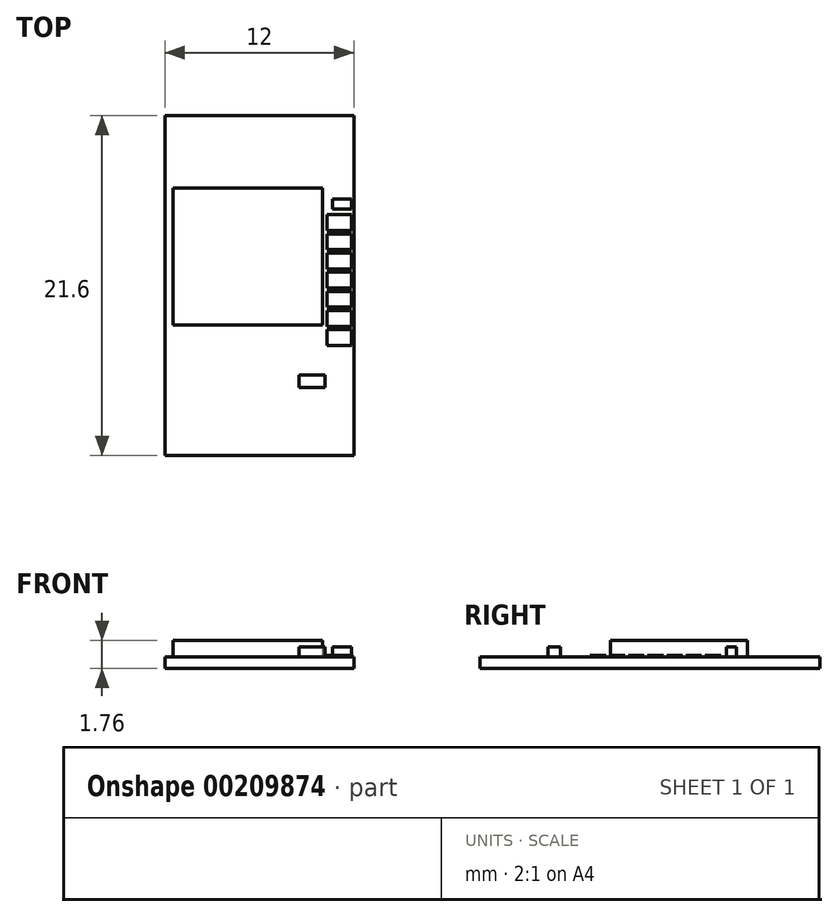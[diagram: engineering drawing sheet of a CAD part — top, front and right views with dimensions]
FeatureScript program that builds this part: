
annotation { "Feature Type Name" : "Feature", "Feature Type Description" : "" }
export const myFeature = defineFeature(function(context is Context, id is Id, definition is map)
    precondition{}
    {
        {
            var Q0;
            Q0=qCreatedBy(makeId("Top.planeOp"),FACE);
            var sketch = newSketch(context, id + "F0", { "sketchPlane" : qUnion([Q0])});
            skLineSegment(sketch, "E0.bottom", {"start": v(6, -10.8) * mm, "end": v(-6, -10.8) * mm});
            skLineSegment(sketch, "E0.top", {"start": v(6, 10.8) * mm, "end": v(-6, 10.8) * mm});
            skLineSegment(sketch, "E0.left", {"start": v(6, -10.8) * mm, "end": v(6, 10.8) * mm});
            skLineSegment(sketch, "E0.right", {"start": v(-6, -10.8) * mm, "end": v(-6, 10.8) * mm});
            skPoint(sketch, "E0.middle", {"position": v(0, 0) * mm});
            skSolve(sketch);
        }
        {
            var Q0;
            Q0 = qSketchRegion(id + "F0", true);
            extrude(context, id + "F1", {"entities" : qUnion([Q0]), "depth" : .72 * mm});
        }
        {
            var Q0;
            Q0=makeQuery(id+"F1.opExtrude","CAP_FACE",FACE,{"disambiguationData":[OSD([sQuery(id+"F0.wireOp",EDGE,"E0.bottom"),sQuery(id+"F0.wireOp",EDGE,"E0.top"),sQuery(id+"F0.wireOp",EDGE,"E0.left"),sQuery(id+"F0.wireOp",EDGE,"E0.right")])],"isStart":false});
            var sketch = newSketch(context, id + "F2", { "sketchPlane" : qUnion([Q0])});
            skLineSegment(sketch, "E1.0", {"start": v(4.1, 4.5) * mm, "end": v(-6, 4.5) * mm, "construction": true});
            skLineSegment(sketch, "E2.0", {"start": v(5.85, -10.8) * mm, "end": v(5.85, -3.8) * mm, "construction": true});
            skLineSegment(sketch, "E3.bottom", {"start": v(5.85, 4.5) * mm, "end": v(4.3, 4.5) * mm});
            skLineSegment(sketch, "E3.top", {"start": v(5.85, 3.5) * mm, "end": v(4.3, 3.5) * mm});
            skLineSegment(sketch, "E3.left", {"start": v(5.85, 4.5) * mm, "end": v(5.85, 3.5) * mm});
            skLineSegment(sketch, "E3.right", {"start": v(4.3, 4.5) * mm, "end": v(4.3, 3.5) * mm});
            skLineSegment(sketch, "E4.0", {"start": v(6, -3.8) * mm, "end": v(5.85, -3.8) * mm, "construction": true});
            skLineSegment(sketch, "E5", {"start": v(-6, 4.5) * mm, "end": v(-6, -3.8) * mm, "construction": true});
            skLineSegment(sketch, "E6", {"start": v(-6, 0.35) * mm, "end": v(1.33, 0.35) * mm, "construction": true});
            skLineSegment(sketch, "E7.MirrorCS", {"start": v(4.3, -3.8) * mm, "end": v(4.3, -2.8) * mm});
            skLineSegment(sketch, "E8.MirrorCS", {"start": v(5.85, -2.8) * mm, "end": v(4.3, -2.8) * mm});
            skLineSegment(sketch, "E9", {"start": v(4.3, -3.8) * mm, "end": v(5.85, -3.8) * mm});
            skLineSegment(sketch, "E10", {"start": v(5.85, -2.8) * mm, "end": v(5.85, -3.8) * mm});
            skLineSegment(sketch, "E11.trimOffspring", {"start": v(5.85, 4.5) * mm, "end": v(5.85, 10.8) * mm, "construction": true});
            skLineSegment(sketch, "E12.trimOffspring", {"start": v(5.85, -2.8) * mm, "end": v(5.85, 3.5) * mm, "construction": true});
            skLineSegment(sketch, "E13.trimOffspring", {"start": v(4.3, -3.8) * mm, "end": v(-6, -3.8) * mm, "construction": true});
            skLineSegment(sketch, "E14.0.1.0", {"start": v(5.85, 3.28) * mm, "end": v(5.85, 2.28) * mm});
            skLineSegment(sketch, "E14.0.1.1", {"start": v(5.85, 3.28) * mm, "end": v(4.3, 3.28) * mm});
            skLineSegment(sketch, "E14.0.1.2", {"start": v(4.3, 3.28) * mm, "end": v(4.3, 2.28) * mm});
            skLineSegment(sketch, "E14.0.1.3", {"start": v(5.85, 2.28) * mm, "end": v(4.3, 2.28) * mm});
            skLineSegment(sketch, "E14.0.2.0", {"start": v(5.85, 2.07) * mm, "end": v(5.85, 1.07) * mm});
            skLineSegment(sketch, "E14.0.2.1", {"start": v(5.85, 2.07) * mm, "end": v(4.3, 2.07) * mm});
            skLineSegment(sketch, "E14.0.2.2", {"start": v(4.3, 2.07) * mm, "end": v(4.3, 1.07) * mm});
            skLineSegment(sketch, "E14.0.2.3", {"start": v(5.85, 1.07) * mm, "end": v(4.3, 1.07) * mm});
            skLineSegment(sketch, "E14.0.3.0", {"start": v(5.85, 0.85) * mm, "end": v(5.85, -0.15) * mm});
            skLineSegment(sketch, "E14.0.3.1", {"start": v(5.85, 0.85) * mm, "end": v(4.3, 0.85) * mm});
            skLineSegment(sketch, "E14.0.3.2", {"start": v(4.3, 0.85) * mm, "end": v(4.3, -0.15) * mm});
            skLineSegment(sketch, "E14.0.3.3", {"start": v(5.85, -0.15) * mm, "end": v(4.3, -0.15) * mm});
            skLineSegment(sketch, "E14.0.4.0", {"start": v(5.85, -0.37) * mm, "end": v(5.85, -1.37) * mm});
            skLineSegment(sketch, "E14.0.4.1", {"start": v(5.85, -0.37) * mm, "end": v(4.3, -0.37) * mm});
            skLineSegment(sketch, "E14.0.4.2", {"start": v(4.3, -0.37) * mm, "end": v(4.3, -1.37) * mm});
            skLineSegment(sketch, "E14.0.4.3", {"start": v(5.85, -1.37) * mm, "end": v(4.3, -1.37) * mm});
            skLineSegment(sketch, "E14.0.5.0", {"start": v(5.85, -1.58) * mm, "end": v(5.85, -2.58) * mm});
            skLineSegment(sketch, "E14.0.5.1", {"start": v(5.85, -1.58) * mm, "end": v(4.3, -1.58) * mm});
            skLineSegment(sketch, "E14.0.5.2", {"start": v(4.3, -1.58) * mm, "end": v(4.3, -2.58) * mm});
            skLineSegment(sketch, "E14.0.5.3", {"start": v(5.85, -2.58) * mm, "end": v(4.3, -2.58) * mm});
            skLineSegment(sketch, "E14.0.6.2", {"start": v(4.3, -2.8) * mm, "end": v(4.3, -3.8) * mm});
            skLineSegment(sketch, "E14.0.6.3", {"start": v(5.85, -3.8) * mm, "end": v(4.3, -3.8) * mm});
            skLineSegment(sketch, "E14.direction1", {"start": v(5.85, 3.5) * mm, "end": v(30.85, 3.5) * mm, "construction": true});
            skLineSegment(sketch, "E14.direction2", {"start": v(5.85, 3.5) * mm, "end": v(5.85, 2.28) * mm, "construction": true});
            skSolve(sketch);
        }
        {
            var Q0;
            Q0 = qSketchRegion(id + "F2", true);
            extrude(context, id + "F3", {"entities" : qUnion([Q0]), "depth" : .1 * mm});
        }
        {
            var Q0;
            Q0=makeQuery(id+"F1.opExtrude","CAP_FACE",FACE,{"disambiguationData":[OSD([sQuery(id+"F0.wireOp",EDGE,"E0.bottom"),sQuery(id+"F0.wireOp",EDGE,"E0.top"),sQuery(id+"F0.wireOp",EDGE,"E0.left"),sQuery(id+"F0.wireOp",EDGE,"E0.right")])],"isStart":false});
            var sketch = newSketch(context, id + "F4", { "sketchPlane" : qUnion([Q0])});
            skLineSegment(sketch, "E15.0", {"start": v(6, 4.87) * mm, "end": v(-6, 4.87) * mm, "construction": true});
            skLineSegment(sketch, "E16.0", {"start": v(5.85, 4.87) * mm, "end": v(5.85, 4.5) * mm, "construction": true});
            skPoint(sketch, "E17.orphan", {"position": v(5.85, 3.5) * mm});
            skLineSegment(sketch, "E18.bottom", {"start": v(5.85, 4.87) * mm, "end": v(4.65, 4.87) * mm});
            skLineSegment(sketch, "E18.top", {"start": v(5.85, 5.5) * mm, "end": v(4.65, 5.5) * mm});
            skLineSegment(sketch, "E18.left", {"start": v(5.85, 4.87) * mm, "end": v(5.85, 5.5) * mm});
            skLineSegment(sketch, "E18.right", {"start": v(4.65, 4.87) * mm, "end": v(4.65, 5.5) * mm});
            skSolve(sketch);
        }
        {
            var Q0;
            Q0 = qSketchRegion(id + "F4", true);
            extrude(context, id + "F5", {"entities" : qUnion([Q0]), "operationType" : NewBodyOperationType.ADD, "depth" : .64 * mm});
        }
        {
            var Q0;
            Q0=makeQuery(id+"F1.opExtrude","CAP_FACE",FACE,{"disambiguationData":[OSD([sQuery(id+"F0.wireOp",EDGE,"E0.bottom"),sQuery(id+"F0.wireOp",EDGE,"E0.top"),sQuery(id+"F0.wireOp",EDGE,"E0.left"),sQuery(id+"F0.wireOp",EDGE,"E0.right")])],"isStart":false});
            var sketch = newSketch(context, id + "F6", { "sketchPlane" : qUnion([Q0])});
            skLineSegment(sketch, "E19.0", {"start": v(4, -10.8) * mm, "end": v(4, 10.8) * mm});
            skLineSegment(sketch, "E20.0", {"start": v(6, 6.2) * mm, "end": v(-6, 6.2) * mm});
            skLineSegment(sketch, "E21.0", {"start": v(6, -2.5) * mm, "end": v(-6, -2.5) * mm});
            skLineSegment(sketch, "E22.0", {"start": v(-5.5, -10.8) * mm, "end": v(-5.5, 10.8) * mm});
            skSolve(sketch);
        }
        {
            var Q0;
            Q0 = qSketchRegion(id + "F6", true);
            extrude(context, id + "F7", {"entities" : qUnion([Q0]), "operationType" : NewBodyOperationType.ADD, "depth" : 1.04 * mm});
        }
        {
            var Q0;
            Q0=makeQuery(id+"F1.opExtrude","CAP_FACE",FACE,{"disambiguationData":[OSD([sQuery(id+"F0.wireOp",EDGE,"E0.bottom"),sQuery(id+"F0.wireOp",EDGE,"E0.top"),sQuery(id+"F0.wireOp",EDGE,"E0.left"),sQuery(id+"F0.wireOp",EDGE,"E0.right")])],"isStart":false});
            var sketch = newSketch(context, id + "F8", { "sketchPlane" : qUnion([Q0])});
            skLineSegment(sketch, "E23.0", {"start": v(6, -5.68) * mm, "end": v(-6, -5.68) * mm});
            skLineSegment(sketch, "E24.0", {"start": v(4.15, -10.8) * mm, "end": v(4.15, 10.8) * mm});
            skLineSegment(sketch, "E25.0", {"start": v(6, -6.48) * mm, "end": v(-6, -6.48) * mm});
            skLineSegment(sketch, "E26.0", {"start": v(2.5, -10.8) * mm, "end": v(2.5, 10.8) * mm});
            skSolve(sketch);
        }
        {
            var Q0;
            Q0 = qSketchRegion(id + "F8", true);
            extrude(context, id + "F9", {"entities" : qUnion([Q0]), "operationType" : NewBodyOperationType.ADD, "depth" : .65 * mm});
        }
        {
            var Q0;
            Q0=makeQuery(id+"F1.opExtrude","CAP_FACE",FACE,{"disambiguationData":[OSD([sQuery(id+"F0.wireOp",EDGE,"E0.bottom"),sQuery(id+"F0.wireOp",EDGE,"E0.top"),sQuery(id+"F0.wireOp",EDGE,"E0.left"),sQuery(id+"F0.wireOp",EDGE,"E0.right")])],"isStart":false});
            var sketch = newSketch(context, id + "F10", { "sketchPlane" : qUnion([Q0])});
            skLineSegment(sketch, "E27.0", {"start": v(5.85, 4.5) * mm, "end": v(4.3, 4.5) * mm, "construction": true});
            skLineSegment(sketch, "E28.0", {"start": v(5.85, -3.8) * mm, "end": v(4.3, -3.8) * mm, "construction": true});
            skLineSegment(sketch, "E29", {"start": v(5.85, -3.8) * mm, "end": v(5.85, 4.5) * mm, "construction": true});
            skLineSegment(sketch, "E30", {"start": v(5.85, 0.35) * mm, "end": v(10.91, 0.35) * mm});
            skPoint(sketch, "E30.endSnap0", {"position": v(5.85, 0.35) * mm});
            skSolve(sketch);
        }
        {
            var Q0;
            Q0=sQuery(id+"F10.wireOp",EDGE,"E29");
            var Q1;
            Q1=sQuery(id+"F10.wireOp",EDGE,"E27.0");
            var Q2;
            Q2=sQuery(id+"F10.wireOp",EDGE,"E28.0");
            var Q3;
            Q3=sQuery(id+"F10.wireOp",EDGE,"E30");
            extrude(context, id + "F11", {"bodyType" : ToolBodyType.SURFACE, "surfaceEntities" : qUnion([Q0, Q1, Q2, Q3]), "endBound" : BoundingType.SYMMETRIC, "depth" : 5 * mm});
        }
        {
            var Q0;
            Q0=makeQuery(id+"F11.opExtrude","SWEPT_BODY",BODY,{"disambiguationData":[OSD([sQuery(id+"F10.wireOp",EDGE,"E30")])]});
            deleteBodies(context, id + "F12", {"entities" : qUnion([Q0])});
        }
    });
